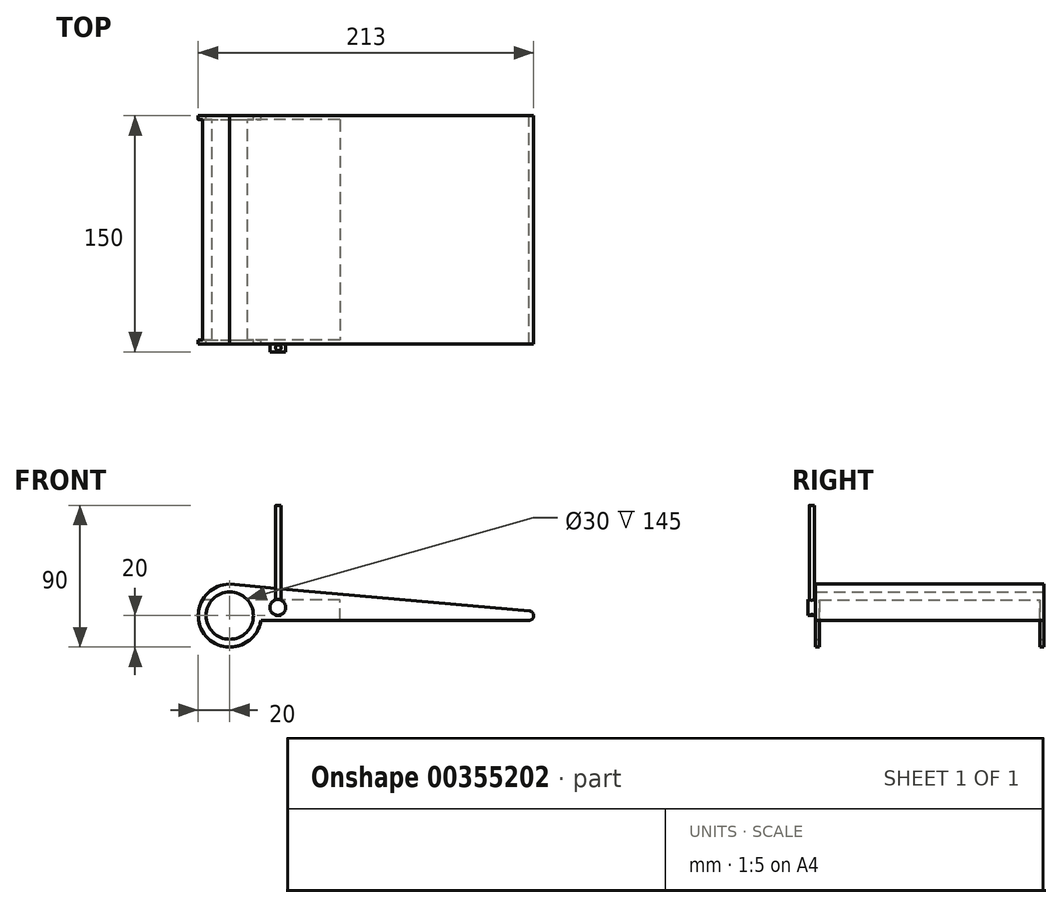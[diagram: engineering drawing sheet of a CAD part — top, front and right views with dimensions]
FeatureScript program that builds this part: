
annotation { "Feature Type Name" : "Feature", "Feature Type Description" : "" }
export const myFeature = defineFeature(function(context is Context, id is Id, definition is map)
    precondition{}
    {
        {
            var Q0;
            Q0=qCreatedBy(makeId("Front.planeOp"),FACE);
            var sketch = newSketch(context, id + "F0", { "sketchPlane" : qUnion([Q0])});
            skCircle(sketch, "E0", {"center": v(0, 0) * mm, "radius": 15 * mm});
            skArc(sketch, "E1", {"start": v(-0.26, 20) * mm, "mid": v(-15.08, -13.14) * mm, "end": v(19.77, -3) * mm});
            skLineSegment(sketch, "E2", {"start": v(0, 0) * mm, "end": v(256.92, 0) * mm, "construction": true});
            skArc(sketch, "E3", {"start": v(189.93, -3) * mm, "mid": v(193, -0.17) * mm, "end": v(190.27, 2.99) * mm});
            skLineSegment(sketch, "E4", {"start": v(-0.26, 20) * mm, "end": v(190.27, 2.99) * mm});
            skLineSegment(sketch, "E5", {"start": v(190.07, -3) * mm, "end": v(19.77, -3) * mm});
            skSolve(sketch);
        }
        {
            var Q0;
            Q0=makeQuery(id+"F0.imprint","IMPRINT",FACE,{"disambiguationData":[TD([[makeQuery(id+"F0.imprint","IMPRINT",EDGE,{"derivedFrom":sQuery(id+"F0.wireOp",EDGE,"E0")}),-1.0]])]});
            extrude(context, id + "F1", {"entities" : qUnion([Q0]), "endBound" : BoundingType.SYMMETRIC, "depth" : 145 * mm});
        }
        {
            var Q0;
            Q0=qCreatedBy(makeId("Right.planeOp"),FACE);
            var sketch = newSketch(context, id + "F2", { "sketchPlane" : qUnion([Q0])});
            skLineSegment(sketch, "E6.bottom", {"start": v(70, -21.72) * mm, "end": v(-70, -21.72) * mm});
            skLineSegment(sketch, "E6.top", {"start": v(70, 10) * mm, "end": v(-70, 10) * mm});
            skLineSegment(sketch, "E6.left", {"start": v(70, -21.72) * mm, "end": v(70, 10) * mm});
            skLineSegment(sketch, "E6.right", {"start": v(-70, -21.72) * mm, "end": v(-70, 10) * mm});
            skSolve(sketch);
        }
        {
            var Q0;
            Q0 = qSketchRegion(id + "F2", true);
            extrude(context, id + "F3", {"entities" : qUnion([Q0]), "operationType" : NewBodyOperationType.REMOVE, "endBound" : BoundingType.SYMMETRIC, "depth" : 140 * mm});
        }
        {
            var Q0;
            Q0=makeQuery(id+"F1.opExtrude","CAP_FACE",FACE,{"disambiguationData":[OSD([sQuery(id+"F0.wireOp",EDGE,"E0"),sQuery(id+"F0.wireOp",EDGE,"E1"),sQuery(id+"F0.wireOp",EDGE,"E3"),sQuery(id+"F0.wireOp",EDGE,"E4"),sQuery(id+"F0.wireOp",EDGE,"E5")])],"isStart":false});
            var sketch = newSketch(context, id + "F4", { "sketchPlane" : qUnion([Q0])});
            skCircle(sketch, "E7", {"center": v(30.5, 5.24) * mm, "radius": 5 * mm});
            skSolve(sketch);
        }
        {
            var Q0;
            Q0 = qSketchRegion(id + "F4", true);
            extrude(context, id + "F5", {"entities" : qUnion([Q0]), "operationType" : NewBodyOperationType.ADD, "depth" : 5 * mm});
        }
        {
            var Q0;
            Q0=qCreatedBy(makeId("Top.planeOp"),FACE);
            var sketch = newSketch(context, id + "F6", { "sketchPlane" : qUnion([Q0])});
            skCircle(sketch, "E8", {"center": v(30.82, -74.85) * mm, "radius": 1.75 * mm});
            skSolve(sketch);
        }
        {
            var Q0;
            Q0 = qSketchRegion(id + "F6", true);
            extrude(context, id + "F7", {"entities" : qUnion([Q0]), "operationType" : NewBodyOperationType.ADD, "depth" : 70 * mm});
        }
    });
